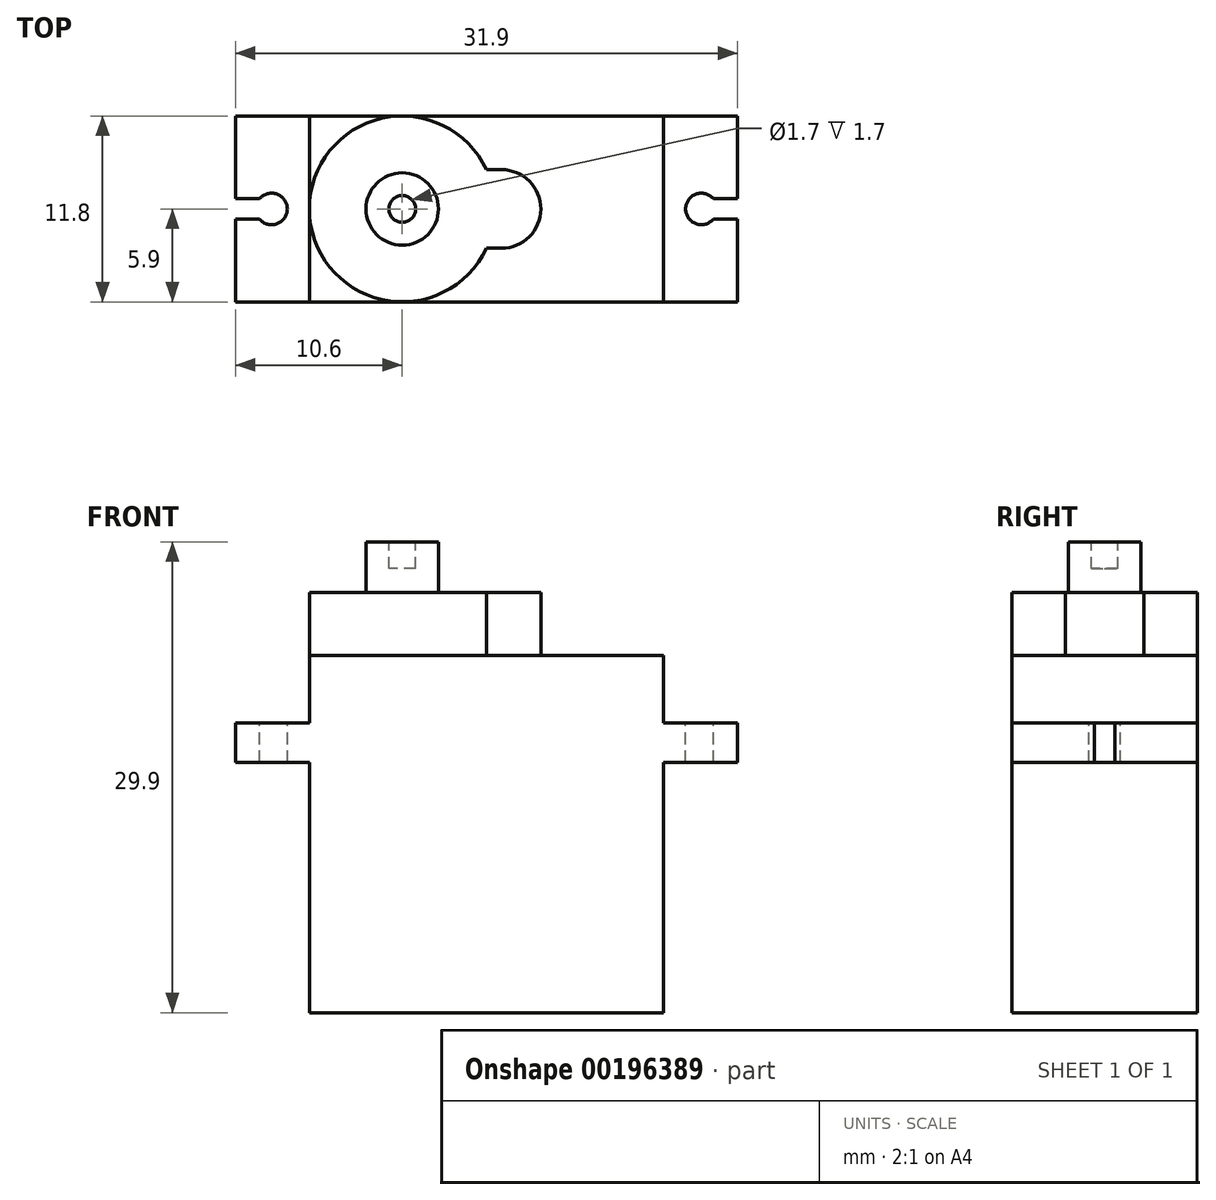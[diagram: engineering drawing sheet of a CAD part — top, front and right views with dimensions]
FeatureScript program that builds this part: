
annotation { "Feature Type Name" : "Feature", "Feature Type Description" : "" }
export const myFeature = defineFeature(function(context is Context, id is Id, definition is map)
    precondition{}
    {
        {
            var Q0;
            Q0=qCreatedBy(makeId("Front.planeOp"),FACE);
            var sketch = newSketch(context, id + "F0", { "sketchPlane" : qUnion([Q0])});
            skLineSegment(sketch, "E0.bottom", {"start": v(0, 0) * mm, "end": v(22.5, 0) * mm});
            skLineSegment(sketch, "E0.top", {"start": v(0, 22.7) * mm, "end": v(22.5, 22.7) * mm});
            skLineSegment(sketch, "E0.left", {"start": v(0, 0) * mm, "end": v(0, 15.9) * mm});
            skLineSegment(sketch, "E0.right", {"start": v(22.5, 0) * mm, "end": v(22.5, 15.9) * mm});
            skLineSegment(sketch, "E1.bottom", {"start": v(-4.7, 18.4) * mm, "end": v(0, 18.4) * mm});
            skLineSegment(sketch, "E1.top", {"start": v(-4.7, 15.9) * mm, "end": v(0, 15.9) * mm});
            skLineSegment(sketch, "E1.left", {"start": v(-4.7, 18.4) * mm, "end": v(-4.7, 15.9) * mm});
            skLineSegment(sketch, "E1.right", {"start": v(27.2, 18.4) * mm, "end": v(27.2, 15.9) * mm});
            skLineSegment(sketch, "E2.trimOffspring", {"start": v(22.5, 15.9) * mm, "end": v(27.2, 15.9) * mm});
            skLineSegment(sketch, "E3.trimOffspring", {"start": v(22.5, 18.4) * mm, "end": v(27.2, 18.4) * mm});
            skLineSegment(sketch, "E4.trimOffspring", {"start": v(0, 18.4) * mm, "end": v(0, 22.7) * mm});
            skLineSegment(sketch, "E5.trimOffspring", {"start": v(22.5, 18.4) * mm, "end": v(22.5, 22.7) * mm});
            skSolve(sketch);
        }
        {
            var Q0;
            Q0 = qSketchRegion(id + "F0", true);
            extrude(context, id + "F1", {"entities" : qUnion([Q0]), "oppositeDirection" : true, "depth" : 11.8 * mm});
        }
        {
            var Q0;
            Q0=makeQuery(id+"F1.opExtrude","SWEPT_FACE",FACE,{"disambiguationData":[OSD([sQuery(id+"F0.wireOp",EDGE,"E0.top")])]});
            var sketch = newSketch(context, id + "F2", { "sketchPlane" : qUnion([Q0])});
            skArc(sketch, "E6", {"start": v(11.24, 8.4) * mm, "mid": v(0, 5.9) * mm, "end": v(11.24, 3.4) * mm});
            skLineSegment(sketch, "E7", {"start": v(5.9, 5.9) * mm, "end": v(22.5, 5.9) * mm, "construction": true});
            skLineSegment(sketch, "E8.bottom", {"start": v(11.24, 8.4) * mm, "end": v(12.2, 8.4) * mm});
            skLineSegment(sketch, "E8.top", {"start": v(11.24, 3.4) * mm, "end": v(12.2, 3.4) * mm});
            skArc(sketch, "E9", {"start": v(12.2, 3.4) * mm, "mid": v(14.7, 5.9) * mm, "end": v(12.2, 8.4) * mm});
            skPoint(sketch, "E10", {"position": v(14.7, 5.9) * mm});
            skPoint(sketch, "E11", {"position": v(4.5, 13.97) * mm});
            skSolve(sketch);
        }
        {
            var Q0;
            Q0 = qSketchRegion(id + "F2", true);
            extrude(context, id + "F3", {"entities" : qUnion([Q0]), "operationType" : NewBodyOperationType.ADD, "depth" : 4 * mm});
        }
        {
            var Q0;
            Q0=makeQuery(id+"F1.opExtrude","SWEPT_FACE",FACE,{"disambiguationData":[OSD([sQuery(id+"F0.wireOp",EDGE,"E3.trimOffspring")])]});
            var sketch = newSketch(context, id + "F4", { "sketchPlane" : qUnion([Q0])});
            skPoint(sketch, "E12", {"position": v(27.2, 5.9) * mm});
            skLineSegment(sketch, "E13.bottom", {"start": v(27.2, 6.55) * mm, "end": v(25.66, 6.55) * mm});
            skLineSegment(sketch, "E13.top", {"start": v(27.2, 5.25) * mm, "end": v(25.66, 5.25) * mm});
            skLineSegment(sketch, "E13.left", {"start": v(27.2, 6.55) * mm, "end": v(27.2, 5.25) * mm});
            skArc(sketch, "E14", {"start": v(25.66, 6.55) * mm, "mid": v(23.9, 5.9) * mm, "end": v(25.66, 5.25) * mm});
            skSolve(sketch);
        }
        {
            var Q0;
            Q0 = qSketchRegion(id + "F4", true);
            extrude(context, id + "F5", {"entities" : qUnion([Q0]), "operationType" : NewBodyOperationType.REMOVE, "oppositeDirection" : true, "depth" : 25 * mm});
        }
        {
            var Q0;
            Q0=makeQuery(id+"F1.opExtrude","SWEPT_FACE",FACE,{"disambiguationData":[OSD([sQuery(id+"F0.wireOp",EDGE,"E1.bottom")])]});
            var sketch = newSketch(context, id + "F6", { "sketchPlane" : qUnion([Q0])});
            skPoint(sketch, "E15", {"position": v(-4.7, 5.9) * mm});
            skLineSegment(sketch, "E16.bottom", {"start": v(-4.7, 6.55) * mm, "end": v(-3.16, 6.55) * mm});
            skLineSegment(sketch, "E16.top", {"start": v(-4.7, 5.25) * mm, "end": v(-3.16, 5.25) * mm});
            skLineSegment(sketch, "E16.left", {"start": v(-4.7, 6.55) * mm, "end": v(-4.7, 5.25) * mm});
            skArc(sketch, "E17", {"start": v(-3.16, 5.25) * mm, "mid": v(-1.4, 5.9) * mm, "end": v(-3.16, 6.55) * mm});
            skSolve(sketch);
        }
        {
            var Q0;
            Q0 = qSketchRegion(id + "F6", true);
            extrude(context, id + "F7", {"entities" : qUnion([Q0]), "operationType" : NewBodyOperationType.REMOVE, "oppositeDirection" : true, "depth" : 25 * mm});
        }
        {
            var Q0;
            Q0=makeQuery(id+"F3.opExtrude","CAP_FACE",FACE,{"disambiguationData":[OSD([sQuery(id+"F2.wireOp",EDGE,"E6"),sQuery(id+"F2.wireOp",EDGE,"E8.bottom"),sQuery(id+"F2.wireOp",EDGE,"E8.top"),sQuery(id+"F2.wireOp",EDGE,"E9")])],"isStart":false});
            var sketch = newSketch(context, id + "F8", { "sketchPlane" : qUnion([Q0])});
            skCircle(sketch, "E18", {"center": v(5.9, 5.9) * mm, "radius": 2.3 * mm});
            skSolve(sketch);
        }
        {
            var Q0;
            Q0 = qSketchRegion(id + "F8", true);
            extrude(context, id + "F9", {"entities" : qUnion([Q0]), "operationType" : NewBodyOperationType.ADD, "depth" : 3.2 * mm});
        }
        {
            var Q0;
            Q0=makeQuery(id+"F9.opExtrude","CAP_FACE",FACE,{"disambiguationData":[OSD([sQuery(id+"F8.wireOp",EDGE,"E18")])],"isStart":false});
            var sketch = newSketch(context, id + "F10", { "sketchPlane" : qUnion([Q0])});
            skCircle(sketch, "E19", {"center": v(5.9, 5.9) * mm, "radius": 0.85 * mm});
            skSolve(sketch);
        }
        {
            var Q0;
            Q0 = qSketchRegion(id + "F10", true);
            extrude(context, id + "F11", {"entities" : qUnion([Q0]), "operationType" : NewBodyOperationType.REMOVE, "oppositeDirection" : true, "depth" : 1.7 * mm});
        }
    });
